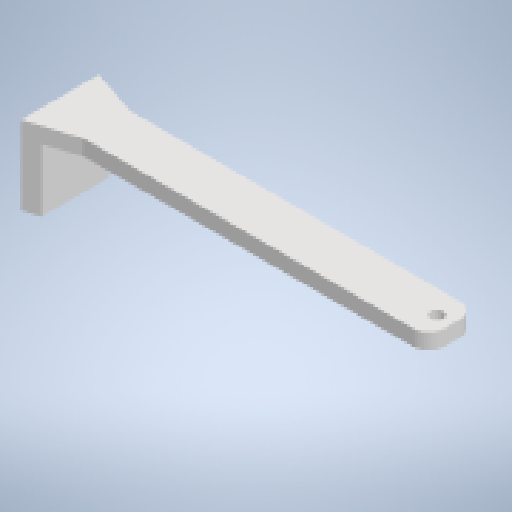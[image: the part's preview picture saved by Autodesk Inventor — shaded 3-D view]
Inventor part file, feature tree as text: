
AUTODESK INVENTOR PART (.ipt)
format: ipt  version: 2024 (Build 280153000, 153)  size: 161,280 bytes
history: native  units: mm
features: extrude x2, sketch x2, fillet x1
ambient origin geometry x8: Origin, YZ Plane, XZ Plane, XY Plane, X Axis, Y Axis, Z Axis, Center Point
bodies: Solido1 (feature_tree)
feature tree (5):
  extrude  "Estrusione1"  Depth=10.0mm
  extrude  "Estrusione2"  Depth=10.0mm
  fillet  "Raccordo1"  Radius=50.0mm
  sketch  "Schizzo1"
  sketch  "Schizzo2"
